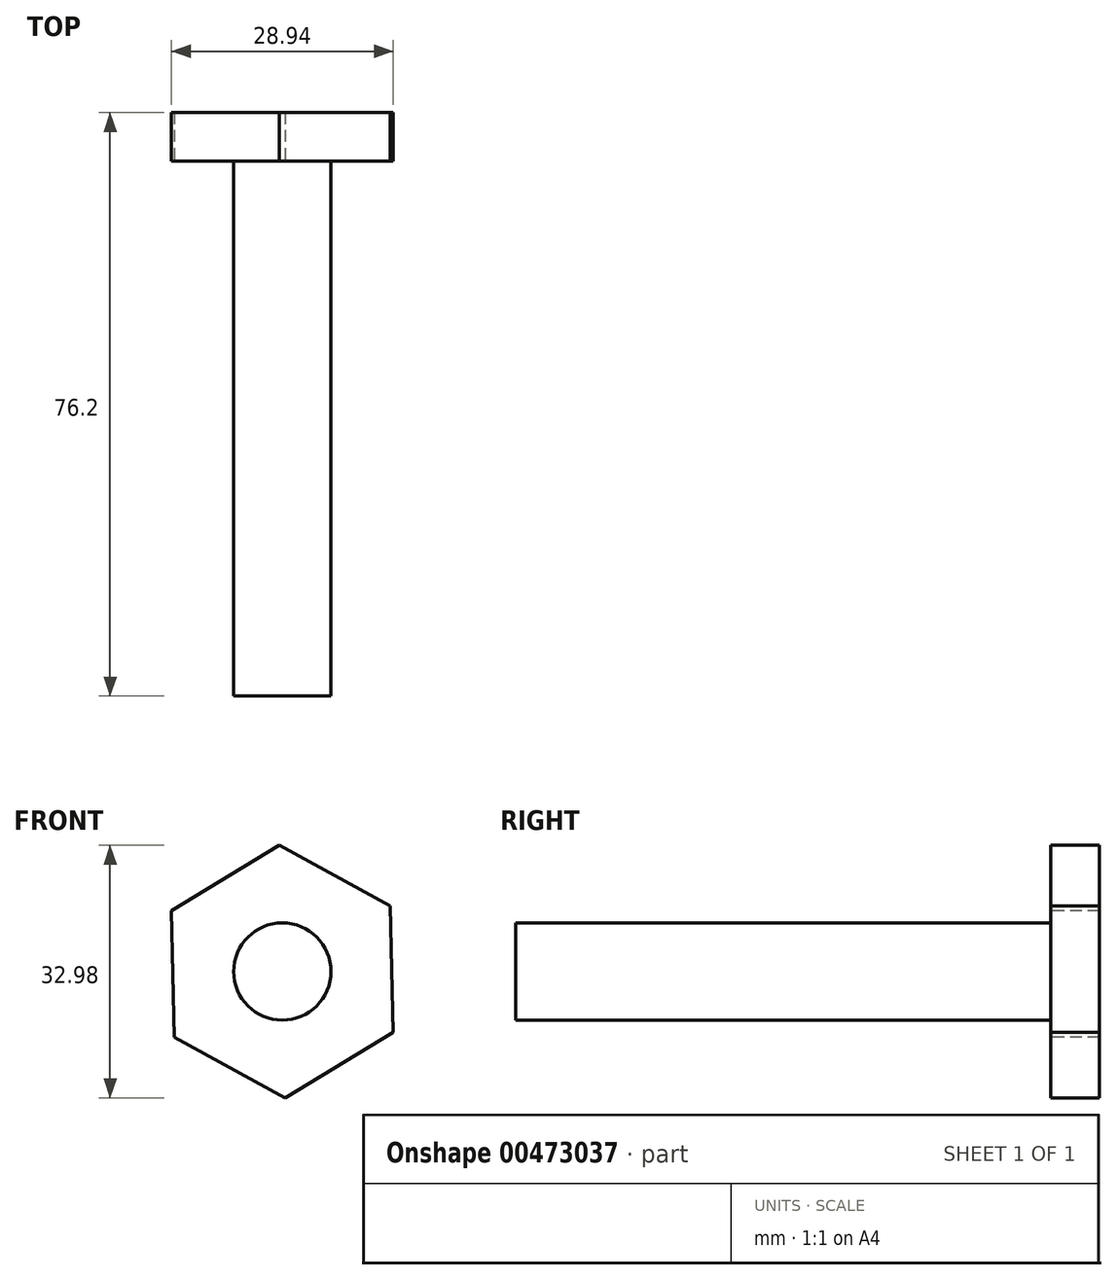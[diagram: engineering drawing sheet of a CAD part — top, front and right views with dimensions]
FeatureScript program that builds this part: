
annotation { "Feature Type Name" : "Feature", "Feature Type Description" : "" }
export const myFeature = defineFeature(function(context is Context, id is Id, definition is map)
    precondition{}
    {
        {
            var Q0;
            Q0=qCreatedBy(makeId("Front.planeOp"),FACE);
            var sketch = newSketch(context, id + "F0", { "sketchPlane" : qUnion([Q0])});
            skCircle(sketch, "E0", {"center": v(0, 0) * mm, "radius": 6.35 * mm});
            skSolve(sketch);
        }
        {
            var Q0;
            Q0=makeQuery(id+"F0.imprint","IMPRINT",FACE,{"disambiguationData":[TD([[makeQuery(id+"F0.imprint","IMPRINT",EDGE,{"derivedFrom":sQuery(id+"F0.wireOp",EDGE,"E0")}),1.0]])]});
            extrude(context, id + "F1", {"entities" : qUnion([Q0]), "depth" : 69.85 * mm});
        }
        {
            var Q0;
            Q0=makeQuery(id+"F1.opExtrude","CAP_FACE",FACE,{"disambiguationData":[OSD([sQuery(id+"F0.wireOp",EDGE,"E0")])],"isStart":true});
            var sketch = newSketch(context, id + "F2", { "sketchPlane" : qUnion([Q0])});
            skCircle(sketch, "E1.cCircle", {"center": v(0, 0) * mm, "radius": 14.29 * mm, "construction": true});
            skLineSegment(sketch, "E1.0", {"start": v(0.38, 16.5) * mm, "end": v(14.47, 7.92) * mm});
            skLineSegment(sketch, "E1.1", {"start": v(14.47, 7.92) * mm, "end": v(14.1, -8.57) * mm});
            skLineSegment(sketch, "E1.2", {"start": v(14.1, -8.57) * mm, "end": v(-0.38, -16.5) * mm});
            skLineSegment(sketch, "E1.3", {"start": v(-0.38, -16.5) * mm, "end": v(-14.47, -7.92) * mm});
            skLineSegment(sketch, "E1.4", {"start": v(-14.47, -7.92) * mm, "end": v(-14.1, 8.57) * mm});
            skLineSegment(sketch, "E1.5", {"start": v(-14.1, 8.57) * mm, "end": v(0.38, 16.5) * mm});
            skPoint(sketch, "E1.0.midPoint", {"position": v(7.43, 12.2) * mm});
            skSolve(sketch);
        }
        {
            var Q0;
            Q0=makeQuery(id+"F2.imprint","IMPRINT",FACE,{"disambiguationData":[TD([[makeQuery(id+"F2.imprint","IMPRINT",EDGE,{"derivedFrom":makeQuery(id+"F1.opExtrude","CAP_EDGE",EDGE,{"disambiguationData":[OSD([sQuery(id+"F0.wireOp",EDGE,"E0")])],"isStart":true})}),-1.0]])]});
            var Q1;
            Q1=makeQuery(id+"F2.imprint","IMPRINT",FACE,{"disambiguationData":[TD([[makeQuery(id+"F2.imprint","IMPRINT",EDGE,{"derivedFrom":sQuery(id+"F2.wireOp",EDGE,"E1.0")}),-1.0]])]});
            extrude(context, id + "F3", {"entities" : qUnion([Q0, Q1]), "operationType" : NewBodyOperationType.ADD, "depth" : 6.35 * mm});
        }
    });
